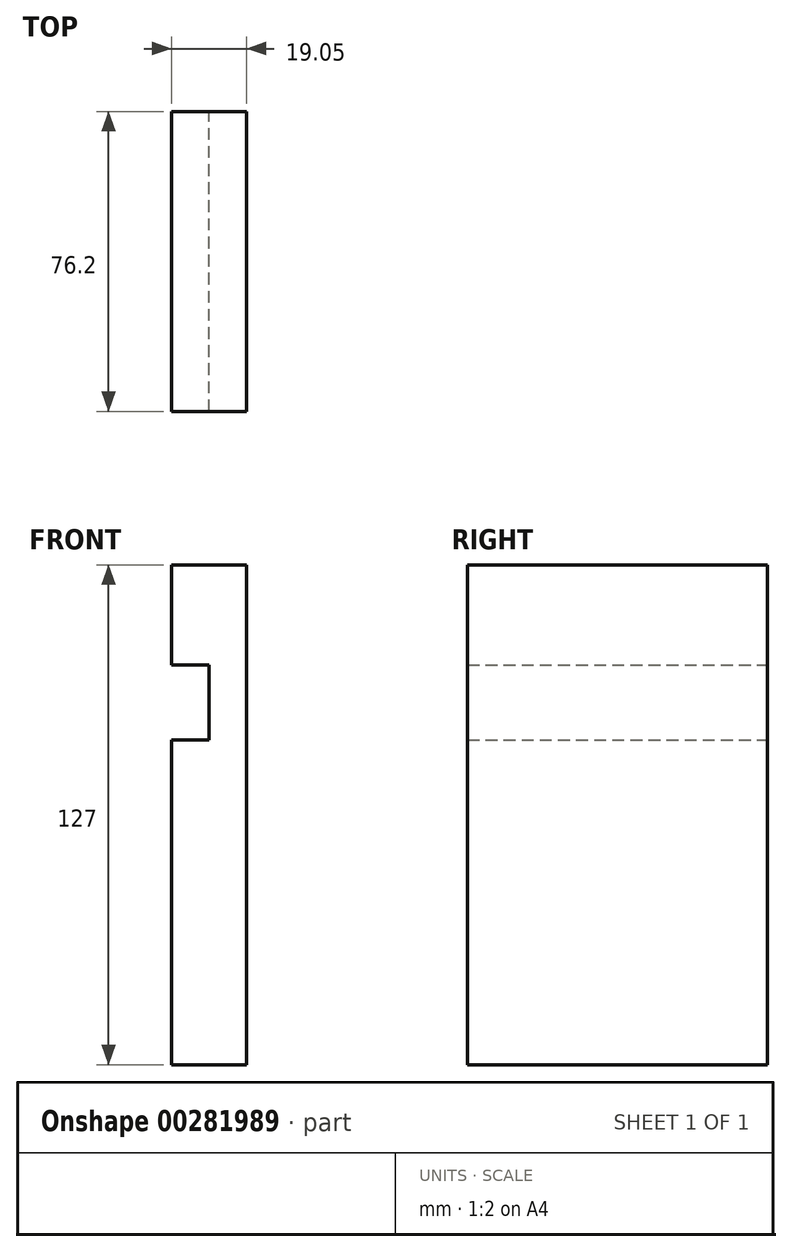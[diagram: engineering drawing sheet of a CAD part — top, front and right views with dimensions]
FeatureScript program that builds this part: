
annotation { "Feature Type Name" : "Feature", "Feature Type Description" : "" }
export const myFeature = defineFeature(function(context is Context, id is Id, definition is map)
    precondition{}
    {
        {
            var Q0;
            Q0=qCreatedBy(makeId("Front.planeOp"),FACE);
            var sketch = newSketch(context, id + "F0", { "sketchPlane" : qUnion([Q0])});
            skLineSegment(sketch, "E0", {"start": v(-22.1, 43.23) * mm, "end": v(-22.1, 68.63) * mm});
            skLineSegment(sketch, "E1", {"start": v(-22.1, 68.63) * mm, "end": v(-3.06, 68.63) * mm});
            skLineSegment(sketch, "E2", {"start": v(-3.06, 68.63) * mm, "end": v(-3.06, -58.37) * mm});
            skLineSegment(sketch, "E3", {"start": v(-3.06, -58.37) * mm, "end": v(-22.1, -58.37) * mm});
            skLineSegment(sketch, "E4", {"start": v(-22.1, -58.37) * mm, "end": v(-22.1, 24.18) * mm});
            skLineSegment(sketch, "E5", {"start": v(-22.1, 24.18) * mm, "end": v(-12.58, 24.18) * mm});
            skLineSegment(sketch, "E6", {"start": v(-12.58, 24.18) * mm, "end": v(-12.58, 43.23) * mm});
            skLineSegment(sketch, "E7", {"start": v(-12.58, 43.23) * mm, "end": v(-22.1, 43.23) * mm});
            skSolve(sketch);
        }
        {
            var Q0;
            Q0 = qSketchRegion(id + "F0", true);
            extrude(context, id + "F1", {"entities" : qUnion([Q0]), "depth" : 76.2 * mm});
        }
    });
